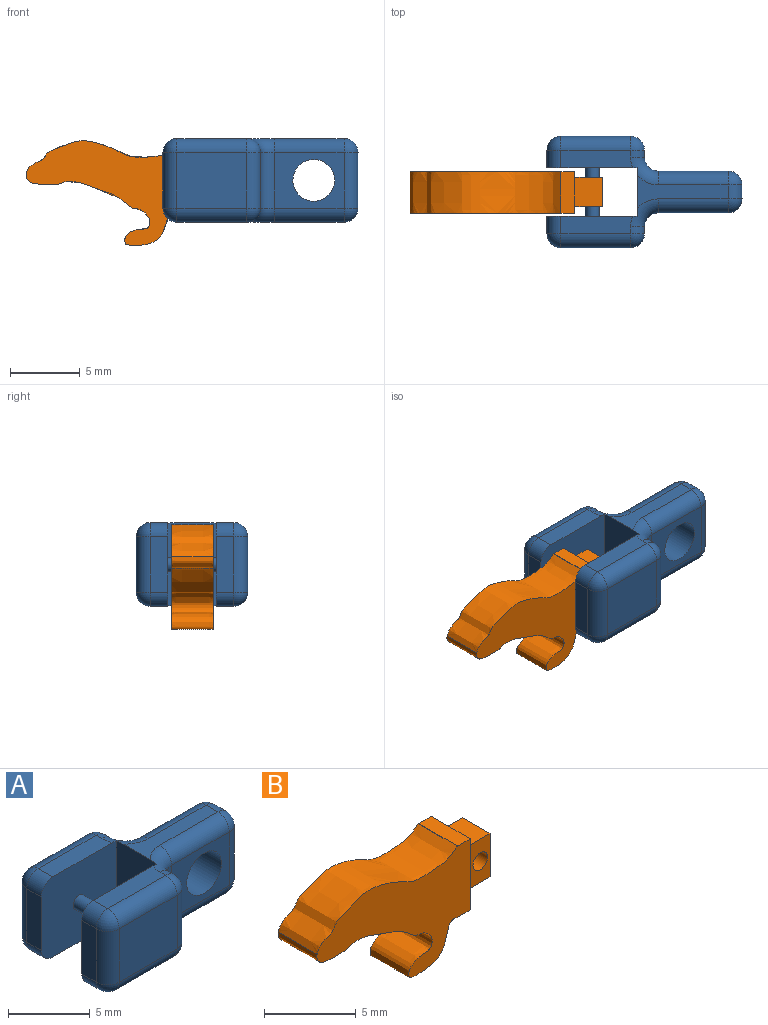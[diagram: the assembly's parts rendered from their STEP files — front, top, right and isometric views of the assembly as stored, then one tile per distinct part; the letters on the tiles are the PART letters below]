
ASSEMBLY  parts=2 mates=1
PART A: 62 faces, bbox 14x8x6.1 mm
  f0: plane 4x1.25mm, normal (-1,0,0), area 5mm2, adj f5,f6,f45,f58
  f1: plane 5.15x1.25mm, normal (0,0,1), area 6.3mm2, adj f5,f7,f46,f47,f58
  f2: plane 6.5x2.35mm, normal (0,0,1), area 7.1mm2, adj f7,f20,f22,f31,f41,f59
  f3: plane 6.5x2.35mm, normal (0,0,-1), area 7.1mm2, adj f8,f28,f33,f43,f52,f59
  f4: plane 5.15x1.25mm, normal (0,0,-1), area 6.3mm2, adj f6,f8,f53,f56,f58
  f5: cylinder r=1mm len=1.25mm, axis (0,-1,0), area 2mm2, adj f0,f1,f40,f58
  f6: cylinder r=1mm len=1.25mm, axis (0,1,0), area 2mm2, adj f0,f4,f49,f58
  f7: torus R=2mm, axis (0,0,1), area 3.3mm2, adj f1,f2,f41,f47,f51,f58,f59
  f8: torus R=2mm, axis (0,0,1), area 3.3mm2, adj f3,f4,f51,f52,f56,f58,f59
  f9: plane 5.15x1.25mm, normal (0,0,1), area 6.3mm2, adj f19,f20,f26,f36,f57
  f10: plane 5.15x1.25mm, normal (0,0,-1), area 6.3mm2, adj f24,f28,f34,f44,f57
  f11: plane 4x1mm, normal (1,0,0), area 4mm2, adj f31,f32,f42,f43
  f12: plane 5x4mm, normal (0,-1,0), area 12.9mm2, adj f41,f42,f51,f52,f60
  f13: plane 5x4mm, normal (0,1,0), area 12.9mm2, adj f22,f23,f32,f33,f60
  f14: plane 4x0.5mm, normal (1,0,0), area 2mm2, adj f19,f23,f24,f25
  f15: plane 5x4mm, normal (0,1,0), area 20mm2, adj f25,f26,f34,f35
  f16: plane 5x4mm, normal (0,-1,0), area 20mm2, adj f45,f46,f53,f54
  f17: plane 4x1.25mm, normal (-1,0,0), area 5mm2, adj f35,f36,f44,f57
  f18: plane 4x0.5mm, normal (1,0,0), area 2mm2, adj f47,f51,f54,f56
  f19: cylinder r=1mm len=1mm, axis (0,1,0), area 0.8mm2, adj f9,f14,f20,f21
  f20: torus R=2mm, axis (0,0,1), area 3.3mm2, adj f2,f9,f19,f22,f23,f57,f59
  f21: sphere r=1mm, area 1.6mm2, adj f19,f25,f26
  f22: cylinder r=1mm len=5mm, axis (-1,0,0), area 7.9mm2, adj f2,f13,f20,f27
  f23: cylinder r=1mm len=4mm, axis (0,0,1), area 6.3mm2, adj f13,f14,f20,f28
  f24: cylinder r=1mm len=1mm, axis (0,-1,0), area 0.8mm2, adj f10,f14,f28,f29
  f25: cylinder r=1mm len=4mm, axis (0,0,-1), area 6.3mm2, adj f14,f15,f21,f29
  f26: cylinder r=1mm len=5mm, axis (-1,0,0), area 7.9mm2, adj f9,f15,f21,f30
  f27: sphere r=1mm, area 1.6mm2, adj f22,f31,f32
  f28: torus R=2mm, axis (0,0,1), area 3.3mm2, adj f3,f10,f23,f24,f33,f57,f59
  f29: sphere r=1mm, area 1.6mm2, adj f24,f25,f34
  f30: sphere r=1mm, area 1.6mm2, adj f26,f35,f36
  f31: cylinder r=1mm len=1mm, axis (0,1,0), area 1.6mm2, adj f2,f11,f27,f37
  f32: cylinder r=1mm len=4mm, axis (0,0,1), area 6.3mm2, adj f11,f13,f27,f38
  f33: cylinder r=1mm len=5mm, axis (1,0,0), area 7.9mm2, adj f3,f13,f28,f38
  f34: cylinder r=1mm len=5mm, axis (1,0,0), area 7.9mm2, adj f10,f15,f29,f39
  f35: cylinder r=1mm len=4mm, axis (0,0,1), area 6.3mm2, adj f15,f17,f30,f39
  f36: cylinder r=1mm len=1.25mm, axis (0,-1,0), area 2mm2, adj f9,f17,f30,f57
  f37: sphere r=1mm, area 1.6mm2, adj f31,f41,f42
  f38: sphere r=1mm, area 1.6mm2, adj f32,f33,f43
  f39: sphere r=1mm, area 1.6mm2, adj f34,f35,f44
  f40: sphere r=1mm, area 1.6mm2, adj f5,f45,f46
  f41: cylinder r=1mm len=5mm, axis (1,0,0), area 7.9mm2, adj f2,f7,f12,f37
  f42: cylinder r=1mm len=4mm, axis (0,0,-1), area 6.3mm2, adj f11,f12,f37,f48
  f43: cylinder r=1mm len=1mm, axis (0,-1,0), area 1.6mm2, adj f3,f11,f38,f48
  f44: cylinder r=1mm len=1.25mm, axis (0,1,0), area 2mm2, adj f10,f17,f39,f57
  f45: cylinder r=1mm len=4mm, axis (0,0,-1), area 6.3mm2, adj f0,f16,f40,f49
  f46: cylinder r=1mm len=5mm, axis (1,0,0), area 7.9mm2, adj f1,f16,f40,f50
  f47: cylinder r=1mm len=1mm, axis (0,1,0), area 0.8mm2, adj f1,f7,f18,f50
  f48: sphere r=1mm, area 1.6mm2, adj f42,f43,f52
  f49: sphere r=1mm, area 1.6mm2, adj f6,f45,f53
  f50: sphere r=1mm, area 1.6mm2, adj f46,f47,f54
  f51: cylinder r=1mm len=4mm, axis (0,0,-1), area 6.3mm2, adj f7,f8,f12,f18
  f52: cylinder r=1mm len=5mm, axis (-1,0,0), area 7.9mm2, adj f3,f8,f12,f48
  f53: cylinder r=1mm len=5mm, axis (-1,0,0), area 7.9mm2, adj f4,f16,f49,f55
  f54: cylinder r=1mm len=4mm, axis (0,0,1), area 6.3mm2, adj f16,f18,f50,f55
  f55: sphere r=1mm, area 1.6mm2, adj f53,f54,f56
  f56: cylinder r=1mm len=1mm, axis (0,-1,0), area 0.8mm2, adj f4,f8,f18,f55
  f57: plane 6.51x6.01mm, normal (0,-1,0), area 37.8mm2, adj f9,f10,f17,f20,f28,f36,f44,f59
  f58: plane 6.51x6.01mm, normal (0,1,0), area 37.8mm2, adj f0,f1,f4,f5,f6,f7,f8,f59
  f59: plane 6.05x3.55mm, normal (-1,0,0), area 21mm2, adj f2,f3,f7,f8,f20,f28,f57,f58
  f60: cylinder r=1.5mm len=3mm, axis (0,-1,0), area 28.3mm2, adj f12,f13
  f61: cylinder r=0.5mm len=3.5mm, axis (0,1,0), area 11mm2, adj f57,f58
PART B: 14 faces, bbox 13.9x3x7.6 mm
  f0: plane 4.75x3mm, normal (1,0,0), area 8.1mm2, adj f4,f5,f6,f7,f8,f9,f10,f11
  f1: plane 3x0.03mm, normal (1,0,0), area 0.1mm2, adj f2,f4,f5,f6
  f2: extruded ~10.82x3mm, area 36.1mm2, adj f1,f3,f4,f5
  f3: extruded ~10.82x5.22mm, area 54.8mm2, adj f2,f4,f5,f7
  f4: plane 11.86x7.6mm, normal (0,-1,0), area 42.7mm2, adj f0,f1,f2,f3,f6,f7
  f5: plane 11.86x7.6mm, normal (0,1,0), area 42.7mm2, adj f0,f1,f2,f3,f6,f7
  f6: plane 3x1mm, normal (0,0,1), area 3mm2, adj f0,f1,f4,f5
  f7: plane 3x1mm, normal (0,0,-1), area 3mm2, adj f0,f3,f4,f5
  f8: plane 2.11x2mm, normal (0,0,1), area 4.2mm2, adj f0,f9,f11,f12
  f9: plane 2.91x2mm, normal (0,-1,0), area 4.8mm2, adj f0,f8,f10,f12,f13
  f10: plane 2.11x2mm, normal (0,0,-1), area 4.2mm2, adj f0,f9,f11,f12
  f11: plane 2.91x2mm, normal (0,1,0), area 4.8mm2, adj f0,f8,f10,f12,f13
  f12: plane 2.91x2.11mm, normal (1,0,0), area 6.1mm2, adj f8,f9,f10,f11
  f13: cylinder r=0.56mm len=2.11mm, axis (0,-1,0), area 7.5mm2, adj f9,f11
PLACE A rot(axis=(0.85,0.21,0.48),0deg) t=(1.61,1.58,0.63)mm
PLACE B t=(-14.52,1.55,12.9)mm
MATE revolute B.f13 <-> A.f61  axis (0,-1,0) through (-3.86,0.08,2.24)mm
